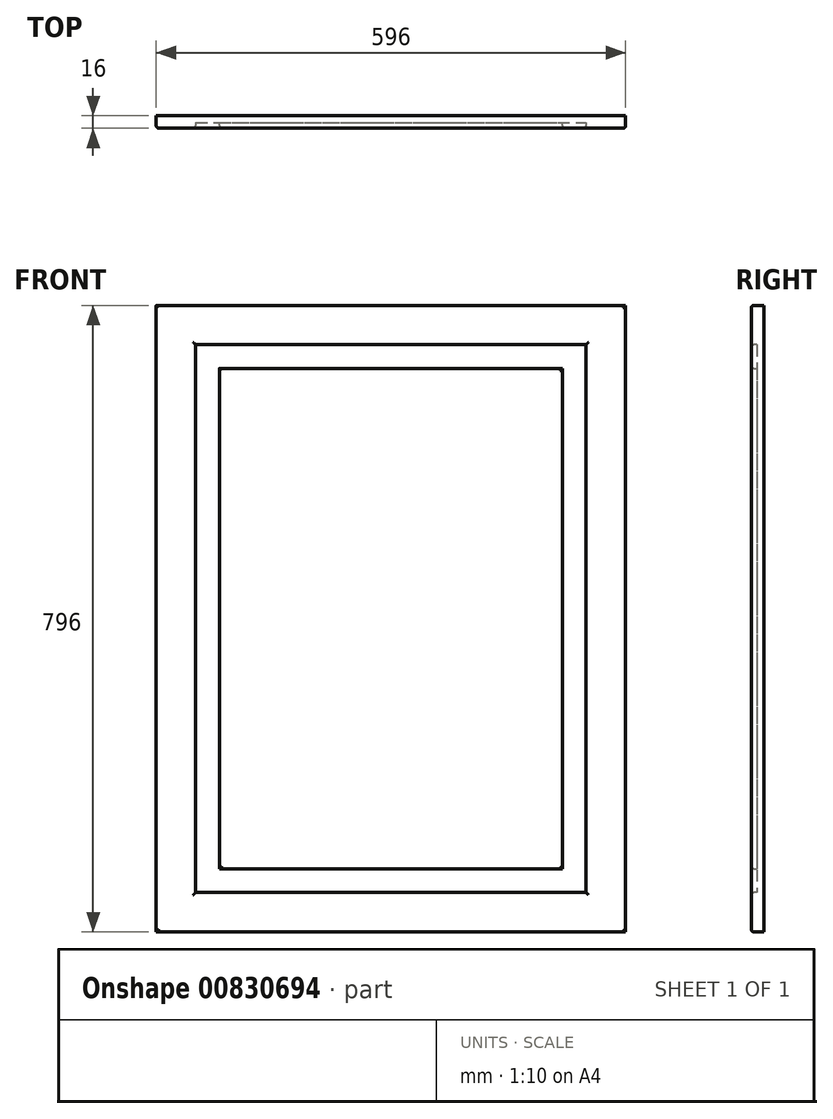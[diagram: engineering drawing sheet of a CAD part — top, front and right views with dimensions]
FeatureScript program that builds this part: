
annotation { "Feature Type Name" : "Feature", "Feature Type Description" : "" }
export const myFeature = defineFeature(function(context is Context, id is Id, definition is map)
    precondition{}
    {
        {
            var Q0;
            Q0=qCreatedBy(makeId("Front.planeOp"),FACE);
            var sketch = newSketch(context, id + "F0", { "sketchPlane" : qUnion([Q0])});
            skLineSegment(sketch, "E0.bottom", {"start": v(0, 0) * mm, "end": v(44.66, 0) * mm});
            skLineSegment(sketch, "E0.top", {"start": v(0, 33.8) * mm, "end": v(44.66, 33.8) * mm});
            skLineSegment(sketch, "E0.left", {"start": v(0, 0) * mm, "end": v(0, 33.8) * mm});
            skLineSegment(sketch, "E0.right", {"start": v(44.66, 0) * mm, "end": v(44.66, 33.8) * mm});
            skSolve(sketch);
        }
        {
            var Q0;
            Q0=makeQuery(id+"F0.imprint","IMPRINT",FACE,{"disambiguationData":[TD([[makeQuery(id+"F0.imprint","IMPRINT",EDGE,{"derivedFrom":sQuery(id+"F0.wireOp",EDGE,"E0.bottom")}),1.0]])]});
            extrude(context, id + "F1", {"entities" : qUnion([Q0]), "depth" : 16 * mm, "offsetDistance" : 25.4 * mm});
        }
        {
            var Q0;
            Q0=makeQuery(id+"F1.opExtrude","SWEPT_FACE",FACE,{"disambiguationData":[OSD([sQuery(id+"F0.wireOp",EDGE,"E0.bottom")])]});
            extrude(context, id + "F2", {"entities" : qUnion([Q0]), "operationType" : NewBodyOperationType.ADD, "oppositeDirection" : true, "depth" : 796 * mm, "offsetDistance" : 25 * mm});
        }
        {
            var Q0;
            {var subQ0=sQuery(id+"F0.wireOp",EDGE,"E0.left");Q0=makeQuery(id+"F2.boolean.opBoolean","MERGE",FACE,{"derivedFrom":[makeQuery(id+"F1.opExtrude","SWEPT_FACE",FACE,{"disambiguationData":[OSD([subQ0])]}),makeQuery(id+"F2.opExtrude","SWEPT_FACE",FACE,{"disambiguationData":[OSD([sQuery(id+"F0.wireOp",EDGE,"E0.bottom"),subQ0])]})]});}
            extrude(context, id + "F3", {"entities" : qUnion([Q0]), "operationType" : NewBodyOperationType.ADD, "oppositeDirection" : true, "depth" : 196 * mm, "offsetDistance" : 25 * mm});
        }
        {
            var Q0;
            {var subQ0=sQuery(id+"F0.wireOp",EDGE,"E0.left");var subQ1=sQuery(id+"F0.wireOp",EDGE,"E0.bottom");Q0=makeQuery(id+"F3.boolean.opBoolean","MERGE",FACE,{"derivedFrom":[makeQuery(id+"F2.boolean.opBoolean","MERGE",FACE,{"derivedFrom":[makeQuery(id+"F1.opExtrude","CAP_FACE",FACE,{"disambiguationData":[OSD([subQ1,sQuery(id+"F0.wireOp",EDGE,"E0.top"),subQ0,sQuery(id+"F0.wireOp",EDGE,"E0.right")])],"isStart":false}),makeQuery(id+"F2.opExtrude","SWEPT_FACE",FACE,{"disambiguationData":[OSD([subQ1]),TDD([makeQuery(id+"F1.opExtrude","CAP_EDGE",EDGE,{"disambiguationData":[OSD([subQ1])],"isStart":false})])]})]}),makeQuery(id+"F3.opExtrude","SWEPT_FACE",FACE,{"disambiguationData":[OSD([subQ1,subQ0]),TDD([makeQuery(id+"F2.boolean.opBoolean","MERGE",EDGE,{"derivedFrom":[makeQuery(id+"F1.opExtrude","CAP_EDGE",EDGE,{"disambiguationData":[OSD([subQ0])],"isStart":false}),makeQuery(id+"F2.opExtrude","SWEPT_EDGE",EDGE,{"disambiguationData":[OSD([subQ1,subQ0]),TDD([makeQuery(id+"F1.opExtrude","CAP_VERTEX",VERTEX,{"disambiguationData":[OSD([subQ1,subQ0])],"isStart":false})])]})]})])]})]});}
            var sketch = newSketch(context, id + "F4", { "sketchPlane" : qUnion([Q0])});
            skLineSegment(sketch, "E1.bottom", {"start": v(59.7, 646.67) * mm, "end": v(128.66, 646.67) * mm});
            skLineSegment(sketch, "E1.top", {"start": v(59.7, 152.97) * mm, "end": v(128.66, 152.97) * mm});
            skLineSegment(sketch, "E1.left", {"start": v(59.7, 646.67) * mm, "end": v(59.7, 152.97) * mm});
            skLineSegment(sketch, "E1.right", {"start": v(128.66, 646.67) * mm, "end": v(128.66, 152.97) * mm});
            skSolve(sketch);
        }
        {
            var Q0;
            Q0=makeQuery(id+"F4.imprint","IMPRINT",FACE,{"disambiguationData":[TD([[makeQuery(id+"F4.imprint","IMPRINT",EDGE,{"derivedFrom":sQuery(id+"F4.wireOp",EDGE,"E1.bottom")}),-1.0]])]});
            extrude(context, id + "F5", {"entities" : qUnion([Q0]), "operationType" : NewBodyOperationType.REMOVE, "oppositeDirection" : true, "depth" : 7 * mm, "offsetDistance" : 25 * mm});
        }
        {
            var Q0;
            Q0=makeQuery(id+"F5.boolean.opBoolean","COPY",FACE,{"derivedFrom":makeQuery(id+"F5.opExtrude","SWEPT_FACE",FACE,{"disambiguationData":[OSD([sQuery(id+"F4.wireOp",EDGE,"E1.left")])]})});
            extrude(context, id + "F6", {"entities" : qUnion([Q0]), "operationType" : NewBodyOperationType.REMOVE, "oppositeDirection" : true, "depth" : 9.7 * mm, "offsetDistance" : 25 * mm});
        }
        {
            var Q0;
            {var subQ0=sQuery(id+"F4.wireOp",EDGE,"E1.bottom");Q0=makeQuery(id+"F6.boolean.opBoolean","MERGE",FACE,{"derivedFrom":[makeQuery(id+"F5.boolean.opBoolean","COPY",FACE,{"derivedFrom":makeQuery(id+"F5.opExtrude","SWEPT_FACE",FACE,{"disambiguationData":[OSD([subQ0])]})}),makeQuery(id+"F6.opExtrude","SWEPT_FACE",FACE,{"disambiguationData":[OSD([subQ0,sQuery(id+"F4.wireOp",EDGE,"E1.left")])]})]});}
            extrude(context, id + "F7", {"entities" : qUnion([Q0]), "operationType" : NewBodyOperationType.ADD, "oppositeDirection" : true, "depth" : 99.33 * mm, "offsetDistance" : 25 * mm});
        }
        {
            var Q0;
            {var subQ0=sQuery(id+"F4.wireOp",EDGE,"E1.bottom");Q0=makeQuery(id+"F6.boolean.opBoolean","MERGE",FACE,{"derivedFrom":[makeQuery(id+"F5.boolean.opBoolean","COPY",FACE,{"derivedFrom":makeQuery(id+"F5.opExtrude","SWEPT_FACE",FACE,{"disambiguationData":[OSD([subQ0])]})}),makeQuery(id+"F6.opExtrude","SWEPT_FACE",FACE,{"disambiguationData":[OSD([subQ0,sQuery(id+"F4.wireOp",EDGE,"E1.left")])]})]});}
            extrude(context, id + "F8", {"entities" : qUnion([Q0]), "operationType" : NewBodyOperationType.REMOVE, "oppositeDirection" : true, "depth" : 99.33 * mm, "offsetDistance" : 25 * mm});
        }
        {
            var Q0;
            {var subQ0=sQuery(id+"F4.wireOp",EDGE,"E1.right");Q0=makeQuery(id+"F8.boolean.opBoolean","MERGE",FACE,{"derivedFrom":[makeQuery(id+"F5.boolean.opBoolean","COPY",FACE,{"derivedFrom":makeQuery(id+"F5.opExtrude","SWEPT_FACE",FACE,{"disambiguationData":[OSD([subQ0])]})}),makeQuery(id+"F8.opExtrude","SWEPT_FACE",FACE,{"disambiguationData":[OSD([sQuery(id+"F4.wireOp",EDGE,"E1.bottom"),subQ0])]})]});}
            extrude(context, id + "F9", {"entities" : qUnion([Q0]), "operationType" : NewBodyOperationType.REMOVE, "oppositeDirection" : true, "depth" : 17.34 * mm, "offsetDistance" : 25 * mm});
        }
        {
            var Q0;
            {var subQ0=sQuery(id+"F4.wireOp",EDGE,"E1.top");Q0=makeQuery(id+"F9.boolean.opBoolean","MERGE",FACE,{"derivedFrom":[makeQuery(id+"F6.boolean.opBoolean","MERGE",FACE,{"derivedFrom":[makeQuery(id+"F5.boolean.opBoolean","COPY",FACE,{"derivedFrom":makeQuery(id+"F5.opExtrude","SWEPT_FACE",FACE,{"disambiguationData":[OSD([subQ0])]})}),makeQuery(id+"F6.opExtrude","SWEPT_FACE",FACE,{"disambiguationData":[OSD([subQ0,sQuery(id+"F4.wireOp",EDGE,"E1.left")])]})]}),makeQuery(id+"F9.opExtrude","SWEPT_FACE",FACE,{"disambiguationData":[OSD([subQ0,sQuery(id+"F4.wireOp",EDGE,"E1.right")])]})]});}
            extrude(context, id + "F10", {"entities" : qUnion([Q0]), "operationType" : NewBodyOperationType.REMOVE, "oppositeDirection" : true, "depth" : 102.97 * mm, "offsetDistance" : 25 * mm});
        }
        {
            var Q0;
            {var subQ0=sQuery(id+"F4.wireOp",EDGE,"E1.right");var subQ1=sQuery(id+"F4.wireOp",EDGE,"E1.top");var subQ2=sQuery(id+"F4.wireOp",EDGE,"E1.left");var subQ3=sQuery(id+"F4.wireOp",EDGE,"E1.bottom");Q0=makeQuery(id+"F10.boolean.opBoolean","MERGE",FACE,{"derivedFrom":[makeQuery(id+"F9.boolean.opBoolean","MERGE",FACE,{"derivedFrom":[makeQuery(id+"F8.boolean.opBoolean","MERGE",FACE,{"derivedFrom":[makeQuery(id+"F6.boolean.opBoolean","MERGE",FACE,{"derivedFrom":[makeQuery(id+"F5.boolean.opBoolean","COPY",FACE,{"derivedFrom":makeQuery(id+"F5.opExtrude","CAP_FACE",FACE,{"disambiguationData":[OSD([subQ3,subQ1,subQ2,subQ0])],"isStart":false})}),makeQuery(id+"F6.opExtrude","SWEPT_FACE",FACE,{"disambiguationData":[OSD([subQ2]),TDD([makeQuery(id+"F5.boolean.opBoolean","COPY",EDGE,{"derivedFrom":makeQuery(id+"F5.opExtrude","CAP_EDGE",EDGE,{"disambiguationData":[OSD([subQ2])],"isStart":false})})])]})]}),makeQuery(id+"F8.opExtrude","SWEPT_FACE",FACE,{"disambiguationData":[OSD([subQ3,subQ2]),TDD([makeQuery(id+"F6.boolean.opBoolean","MERGE",EDGE,{"derivedFrom":[makeQuery(id+"F5.boolean.opBoolean","COPY",EDGE,{"derivedFrom":makeQuery(id+"F5.opExtrude","CAP_EDGE",EDGE,{"disambiguationData":[OSD([subQ3])],"isStart":false})}),makeQuery(id+"F6.opExtrude","SWEPT_EDGE",EDGE,{"disambiguationData":[OSD([subQ3,subQ2]),TDD([makeQuery(id+"F5.boolean.opBoolean","COPY",VERTEX,{"derivedFrom":makeQuery(id+"F5.opExtrude","CAP_VERTEX",VERTEX,{"disambiguationData":[OSD([subQ3,subQ2])],"isStart":false})})])]})]})])]})]}),makeQuery(id+"F9.opExtrude","SWEPT_FACE",FACE,{"disambiguationData":[OSD([subQ3,subQ0]),TDD([makeQuery(id+"F8.boolean.opBoolean","MERGE",EDGE,{"derivedFrom":[makeQuery(id+"F5.boolean.opBoolean","COPY",EDGE,{"derivedFrom":makeQuery(id+"F5.opExtrude","CAP_EDGE",EDGE,{"disambiguationData":[OSD([subQ0])],"isStart":false})}),makeQuery(id+"F8.opExtrude","SWEPT_EDGE",EDGE,{"disambiguationData":[OSD([subQ3,subQ0]),TDD([makeQuery(id+"F5.boolean.opBoolean","COPY",VERTEX,{"derivedFrom":makeQuery(id+"F5.opExtrude","CAP_VERTEX",VERTEX,{"disambiguationData":[OSD([subQ3,subQ0])],"isStart":false})})])]})]})])]})]}),makeQuery(id+"F10.opExtrude","SWEPT_FACE",FACE,{"disambiguationData":[OSD([subQ1,subQ2,subQ0]),TDD([makeQuery(id+"F9.boolean.opBoolean","MERGE",EDGE,{"derivedFrom":[makeQuery(id+"F6.boolean.opBoolean","MERGE",EDGE,{"derivedFrom":[makeQuery(id+"F5.boolean.opBoolean","COPY",EDGE,{"derivedFrom":makeQuery(id+"F5.opExtrude","CAP_EDGE",EDGE,{"disambiguationData":[OSD([subQ1])],"isStart":false})}),makeQuery(id+"F6.opExtrude","SWEPT_EDGE",EDGE,{"disambiguationData":[OSD([subQ1,subQ2]),TDD([makeQuery(id+"F5.boolean.opBoolean","COPY",VERTEX,{"derivedFrom":makeQuery(id+"F5.opExtrude","CAP_VERTEX",VERTEX,{"disambiguationData":[OSD([subQ1,subQ2])],"isStart":false})})])]})]}),makeQuery(id+"F9.opExtrude","SWEPT_EDGE",EDGE,{"disambiguationData":[OSD([subQ1,subQ0]),TDD([makeQuery(id+"F5.boolean.opBoolean","COPY",VERTEX,{"derivedFrom":makeQuery(id+"F5.opExtrude","CAP_VERTEX",VERTEX,{"disambiguationData":[OSD([subQ1,subQ0])],"isStart":false})})])]})]})])]})]});}
            var sketch = newSketch(context, id + "F11", { "sketchPlane" : qUnion([Q0])});
            skLineSegment(sketch, "E2.bottom", {"start": v(74.13, 678.73) * mm, "end": v(109.41, 678.73) * mm});
            skLineSegment(sketch, "E2.top", {"start": v(74.13, 186.63) * mm, "end": v(109.41, 186.63) * mm});
            skLineSegment(sketch, "E2.left", {"start": v(74.13, 678.73) * mm, "end": v(74.13, 186.63) * mm});
            skLineSegment(sketch, "E2.right", {"start": v(109.41, 678.73) * mm, "end": v(109.41, 186.63) * mm});
            skSolve(sketch);
        }
        {
            var Q0;
            Q0=makeQuery(id+"F11.imprint","IMPRINT",FACE,{"disambiguationData":[TD([[makeQuery(id+"F11.imprint","IMPRINT",EDGE,{"derivedFrom":sQuery(id+"F11.wireOp",EDGE,"E2.bottom")}),-1.0]])]});
            extrude(context, id + "F12", {"entities" : qUnion([Q0]), "operationType" : NewBodyOperationType.ADD, "depth" : 7 * mm, "offsetDistance" : 25 * mm});
        }
        {
            var Q0;
            Q0=makeQuery(id+"F12.opExtrude","SWEPT_FACE",FACE,{"disambiguationData":[OSD([sQuery(id+"F11.wireOp",EDGE,"E2.bottom")])]});
            extrude(context, id + "F13", {"entities" : qUnion([Q0]), "operationType" : NewBodyOperationType.ADD, "depth" : 37.27 * mm, "offsetDistance" : 25 * mm});
        }
        {
            var Q0;
            {var subQ0=sQuery(id+"F11.wireOp",EDGE,"E2.right");Q0=makeQuery(id+"F13.boolean.opBoolean","MERGE",FACE,{"derivedFrom":[makeQuery(id+"F12.opExtrude","SWEPT_FACE",FACE,{"disambiguationData":[OSD([subQ0])]}),makeQuery(id+"F13.opExtrude","SWEPT_FACE",FACE,{"disambiguationData":[OSD([sQuery(id+"F11.wireOp",EDGE,"E2.bottom"),subQ0])]})]});}
            extrude(context, id + "F14", {"entities" : qUnion([Q0]), "operationType" : NewBodyOperationType.ADD, "depth" : 6.58 * mm, "offsetDistance" : 25 * mm});
        }
        {
            var Q0;
            {var subQ0=sQuery(id+"F11.wireOp",EDGE,"E2.top");Q0=makeQuery(id+"F14.boolean.opBoolean","MERGE",FACE,{"derivedFrom":[makeQuery(id+"F12.opExtrude","SWEPT_FACE",FACE,{"disambiguationData":[OSD([subQ0])]}),makeQuery(id+"F14.opExtrude","SWEPT_FACE",FACE,{"disambiguationData":[OSD([subQ0,sQuery(id+"F11.wireOp",EDGE,"E2.right")])]})]});}
            extrude(context, id + "F15", {"entities" : qUnion([Q0]), "operationType" : NewBodyOperationType.ADD, "depth" : 106.63 * mm, "offsetDistance" : 25 * mm});
        }
        {
            var Q0;
            {var subQ0=sQuery(id+"F11.wireOp",EDGE,"E2.left");Q0=makeQuery(id+"F15.boolean.opBoolean","MERGE",FACE,{"derivedFrom":[makeQuery(id+"F13.boolean.opBoolean","MERGE",FACE,{"derivedFrom":[makeQuery(id+"F12.opExtrude","SWEPT_FACE",FACE,{"disambiguationData":[OSD([subQ0])]}),makeQuery(id+"F13.opExtrude","SWEPT_FACE",FACE,{"disambiguationData":[OSD([sQuery(id+"F11.wireOp",EDGE,"E2.bottom"),subQ0])]})]}),makeQuery(id+"F15.opExtrude","SWEPT_FACE",FACE,{"disambiguationData":[OSD([sQuery(id+"F11.wireOp",EDGE,"E2.top"),subQ0])]})]});}
            extrude(context, id + "F16", {"entities" : qUnion([Q0]), "operationType" : NewBodyOperationType.REMOVE, "oppositeDirection" : true, "depth" : 5.87 * mm, "offsetDistance" : 25 * mm});
        }
        {
            var Q0;
            Q0=makeQuery(id+"F3.opExtrude","CAP_FACE",FACE,{"disambiguationData":[OSD([sQuery(id+"F0.wireOp",EDGE,"E0.bottom"),sQuery(id+"F0.wireOp",EDGE,"E0.left")])],"isStart":false});
            extrude(context, id + "F17", {"entities" : qUnion([Q0]), "operationType" : NewBodyOperationType.ADD, "depth" : 200 * mm, "offsetDistance" : 25 * mm});
        }
        {
            var Q0;
            {var subQ0=sQuery(id+"F4.wireOp",EDGE,"E1.right");Q0=makeQuery(id+"F10.boolean.opBoolean","MERGE",FACE,{"derivedFrom":[makeQuery(id+"F9.boolean.opBoolean","COPY",FACE,{"derivedFrom":makeQuery(id+"F9.opExtrude","CAP_FACE",FACE,{"disambiguationData":[OSD([sQuery(id+"F4.wireOp",EDGE,"E1.bottom"),subQ0])],"isStart":false})}),makeQuery(id+"F10.opExtrude","SWEPT_FACE",FACE,{"disambiguationData":[OSD([sQuery(id+"F4.wireOp",EDGE,"E1.top"),subQ0])]})]});}
            extrude(context, id + "F18", {"entities" : qUnion([Q0]), "operationType" : NewBodyOperationType.REMOVE, "oppositeDirection" : true, "depth" : 200 * mm, "offsetDistance" : 25 * mm});
        }
        {
            var Q0;
            {var subQ0=sQuery(id+"F11.wireOp",EDGE,"E2.right");var subQ1=sQuery(id+"F11.wireOp",EDGE,"E2.top");Q0=makeQuery(id+"F15.boolean.opBoolean","MERGE",FACE,{"derivedFrom":[makeQuery(id+"F14.opExtrude","CAP_FACE",FACE,{"disambiguationData":[OSD([sQuery(id+"F11.wireOp",EDGE,"E2.bottom"),subQ0])],"isStart":false}),makeQuery(id+"F15.opExtrude","SWEPT_FACE",FACE,{"disambiguationData":[OSD([subQ1,subQ0]),TDD([makeQuery(id+"F14.opExtrude","CAP_EDGE",EDGE,{"disambiguationData":[OSD([subQ1,subQ0])],"isStart":false})])]})]});}
            extrude(context, id + "F19", {"entities" : qUnion([Q0]), "operationType" : NewBodyOperationType.ADD, "depth" : 200 * mm, "offsetDistance" : 25 * mm});
        }
        {
            var Q0;
            Q0=makeQuery(id+"F17.opExtrude","CAP_FACE",FACE,{"disambiguationData":[OSD([sQuery(id+"F0.wireOp",EDGE,"E0.bottom"),sQuery(id+"F0.wireOp",EDGE,"E0.left")])],"isStart":false});
            extrude(context, id + "F20", {"entities" : qUnion([Q0]), "operationType" : NewBodyOperationType.ADD, "depth" : 200 * mm, "offsetDistance" : 25 * mm});
        }
        {
            var Q0;
            Q0=makeQuery(id+"F18.boolean.opBoolean","COPY",FACE,{"derivedFrom":makeQuery(id+"F18.opExtrude","CAP_FACE",FACE,{"disambiguationData":[OSD([sQuery(id+"F4.wireOp",EDGE,"E1.bottom"),sQuery(id+"F4.wireOp",EDGE,"E1.top"),sQuery(id+"F4.wireOp",EDGE,"E1.right")])],"isStart":false})});
            extrude(context, id + "F21", {"entities" : qUnion([Q0]), "operationType" : NewBodyOperationType.REMOVE, "oppositeDirection" : true, "depth" : 200 * mm, "offsetDistance" : 25 * mm});
        }
        {
            var Q0;
            Q0=makeQuery(id+"F19.opExtrude","CAP_FACE",FACE,{"disambiguationData":[OSD([sQuery(id+"F11.wireOp",EDGE,"E2.bottom"),sQuery(id+"F11.wireOp",EDGE,"E2.top"),sQuery(id+"F11.wireOp",EDGE,"E2.right")])],"isStart":false});
            extrude(context, id + "F22", {"entities" : qUnion([Q0]), "operationType" : NewBodyOperationType.ADD, "depth" : 200 * mm, "offsetDistance" : 25 * mm});
        }
        {
            var Q0;
            {var subQ0=sQuery(id+"F11.wireOp",EDGE,"E2.right");var subQ1=sQuery(id+"F11.wireOp",EDGE,"E2.top");var subQ2=makeQuery(id+"F12.opExtrude","CAP_VERTEX",VERTEX,{"disambiguationData":[OSD([subQ1,subQ0])],"isStart":false});var subQ3=sQuery(id+"F11.wireOp",EDGE,"E2.bottom");var subQ4=makeQuery(id+"F13.boolean.opBoolean","MERGE",EDGE,{"derivedFrom":[makeQuery(id+"F12.opExtrude","CAP_EDGE",EDGE,{"disambiguationData":[OSD([subQ0])],"isStart":false}),makeQuery(id+"F13.opExtrude","SWEPT_EDGE",EDGE,{"disambiguationData":[OSD([subQ3,subQ0]),TDD([makeQuery(id+"F12.opExtrude","CAP_VERTEX",VERTEX,{"disambiguationData":[OSD([subQ3,subQ0])],"isStart":false})])]})]});var subQ5=makeQuery(id+"F15.boolean.opBoolean","MERGE",EDGE,{"derivedFrom":[makeQuery(id+"F14.opExtrude","CAP_EDGE",EDGE,{"disambiguationData":[OSD([subQ3,subQ0]),TDD([subQ4])],"isStart":false}),makeQuery(id+"F15.opExtrude","SWEPT_EDGE",EDGE,{"disambiguationData":[OSD([subQ1,subQ0]),TDD([makeQuery(id+"F14.opExtrude","CAP_VERTEX",VERTEX,{"disambiguationData":[OSD([subQ1,subQ0]),TDD([subQ2])],"isStart":false})])]})]});Q0=makeQuery(id+"F22.boolean.opBoolean","MERGE",FACE,{"derivedFrom":[makeQuery(id+"F19.boolean.opBoolean","MERGE",FACE,{"derivedFrom":[makeQuery(id+"F15.boolean.opBoolean","MERGE",FACE,{"derivedFrom":[makeQuery(id+"F14.boolean.opBoolean","MERGE",FACE,{"derivedFrom":[makeQuery(id+"F13.boolean.opBoolean","MERGE",FACE,{"derivedFrom":[makeQuery(id+"F12.opExtrude","CAP_FACE",FACE,{"disambiguationData":[OSD([subQ3,subQ1,sQuery(id+"F11.wireOp",EDGE,"E2.left"),subQ0])],"isStart":false}),makeQuery(id+"F13.opExtrude","SWEPT_FACE",FACE,{"disambiguationData":[OSD([subQ3]),TDD([makeQuery(id+"F12.opExtrude","CAP_EDGE",EDGE,{"disambiguationData":[OSD([subQ3])],"isStart":false})])]})]}),makeQuery(id+"F14.opExtrude","SWEPT_FACE",FACE,{"disambiguationData":[OSD([subQ3,subQ0]),TDD([subQ4])]})]}),makeQuery(id+"F15.opExtrude","SWEPT_FACE",FACE,{"disambiguationData":[OSD([subQ1,subQ0]),TDD([makeQuery(id+"F14.boolean.opBoolean","MERGE",EDGE,{"derivedFrom":[makeQuery(id+"F12.opExtrude","CAP_EDGE",EDGE,{"disambiguationData":[OSD([subQ1])],"isStart":false}),makeQuery(id+"F14.opExtrude","SWEPT_EDGE",EDGE,{"disambiguationData":[OSD([subQ1,subQ0]),TDD([subQ2])]})]})])]})]}),makeQuery(id+"F19.opExtrude","SWEPT_FACE",FACE,{"disambiguationData":[OSD([subQ3,subQ1,subQ0]),TDD([subQ5])]})]}),makeQuery(id+"F22.opExtrude","SWEPT_FACE",FACE,{"disambiguationData":[OSD([subQ3,subQ1,subQ0]),TDD([makeQuery(id+"F19.opExtrude","CAP_EDGE",EDGE,{"disambiguationData":[OSD([subQ3,subQ1,subQ0]),TDD([subQ5])],"isStart":false})])]})]});}
            var Q1;
            {var subQ0=sQuery(id+"F0.wireOp",EDGE,"E0.left");var subQ1=sQuery(id+"F0.wireOp",EDGE,"E0.bottom");var subQ2=makeQuery(id+"F2.boolean.opBoolean","MERGE",EDGE,{"derivedFrom":[makeQuery(id+"F1.opExtrude","CAP_EDGE",EDGE,{"disambiguationData":[OSD([subQ0])],"isStart":false}),makeQuery(id+"F2.opExtrude","SWEPT_EDGE",EDGE,{"disambiguationData":[OSD([subQ1,subQ0]),TDD([makeQuery(id+"F1.opExtrude","CAP_VERTEX",VERTEX,{"disambiguationData":[OSD([subQ1,subQ0])],"isStart":false})])]})]});var subQ3=makeQuery(id+"F3.opExtrude","CAP_EDGE",EDGE,{"disambiguationData":[OSD([subQ1,subQ0]),TDD([subQ2])],"isStart":false});Q1=makeQuery(id+"F20.boolean.opBoolean","MERGE",FACE,{"derivedFrom":[makeQuery(id+"F17.boolean.opBoolean","MERGE",FACE,{"derivedFrom":[makeQuery(id+"F3.boolean.opBoolean","MERGE",FACE,{"derivedFrom":[makeQuery(id+"F2.boolean.opBoolean","MERGE",FACE,{"derivedFrom":[makeQuery(id+"F1.opExtrude","CAP_FACE",FACE,{"disambiguationData":[OSD([subQ1,sQuery(id+"F0.wireOp",EDGE,"E0.top"),subQ0,sQuery(id+"F0.wireOp",EDGE,"E0.right")])],"isStart":false}),makeQuery(id+"F2.opExtrude","SWEPT_FACE",FACE,{"disambiguationData":[OSD([subQ1]),TDD([makeQuery(id+"F1.opExtrude","CAP_EDGE",EDGE,{"disambiguationData":[OSD([subQ1])],"isStart":false})])]})]}),makeQuery(id+"F3.opExtrude","SWEPT_FACE",FACE,{"disambiguationData":[OSD([subQ1,subQ0]),TDD([subQ2])]})]}),makeQuery(id+"F17.opExtrude","SWEPT_FACE",FACE,{"disambiguationData":[OSD([subQ1,subQ0]),TDD([subQ3])]})]}),makeQuery(id+"F20.opExtrude","SWEPT_FACE",FACE,{"disambiguationData":[OSD([subQ1,subQ0]),TDD([makeQuery(id+"F17.opExtrude","CAP_EDGE",EDGE,{"disambiguationData":[OSD([subQ1,subQ0]),TDD([subQ3])],"isStart":false})])]})]});}
            fillet(context, id + "F23", {"entities" : qUnion([Q0, Q1]), "radius" : 3 * mm, "tangentPropagation" : true, "allowEdgeOverflow" : false});
        }
    });
